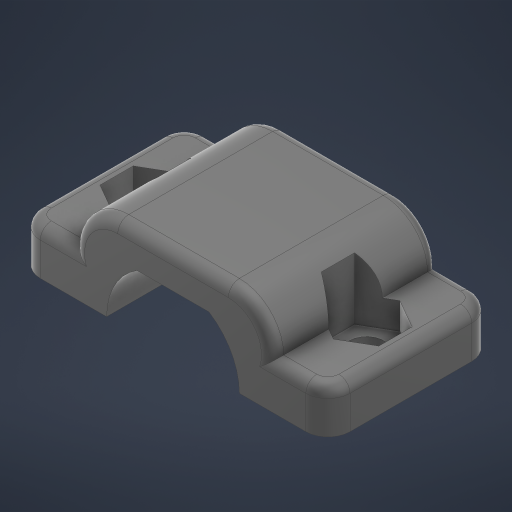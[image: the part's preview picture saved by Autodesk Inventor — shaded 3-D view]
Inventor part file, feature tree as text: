
AUTODESK INVENTOR PART (.ipt)
format: ipt  version: 2024 (Build 280153000, 153)  size: 337,920 bytes
history: native  units: in
note: dims shown in document units (in); Inventor stores cm internally (conversion verified against a paired STEP export)
features: sketch x3, extrude x2, plane x2, fillet x2, hole x1, mirror x1
ambient origin geometry x8: Origin, YZ Plane, XZ Plane, XY Plane, X Axis, Y Axis, Z Axis, Center Point
bodies: Solid1 (feature_tree)
feature tree (11):
  extrude  "Extrusion2"  Depth=0.1181in TaperAngle=0.0deg
  plane  "Work Plane1"
  extrude  "Extrusion3"  Depth=0.1575in
  hole  "Hole1"  [1 undecoded]
  mirror  "Mirror1"
  plane  "Work Plane2"
  fillet  "Fillet3"  Radius=0.2953in
  fillet  "Fillet4"  Radius=0.0787in
  sketch  "Sketch3"  dims[d20=0.1575in d21=0.1969in d22=0.315in d23=0.1181in d24=0.5906in d25=0.0in]
  sketch  "Sketch4"  dims[d26=0.2366in d27=0.1575in]
  sketch  "Sketch5"  dims[d28=0.315in d29=0.0945in d30=0.0in d31=0.0in d32=0.122in d33=0.2362in d34=0.1575in d35=0.0787in d36=90.0deg d37=0.315in d38=0.8108in d39=0.2953in d40=0.2953in d42=0.0787in d43=0.0394in]
note: 1 required parameter value undecoded (feature->parameter linkage not recoverable at this tier; creation-order binding heuristic only, values carry confidence <= 0.55)
